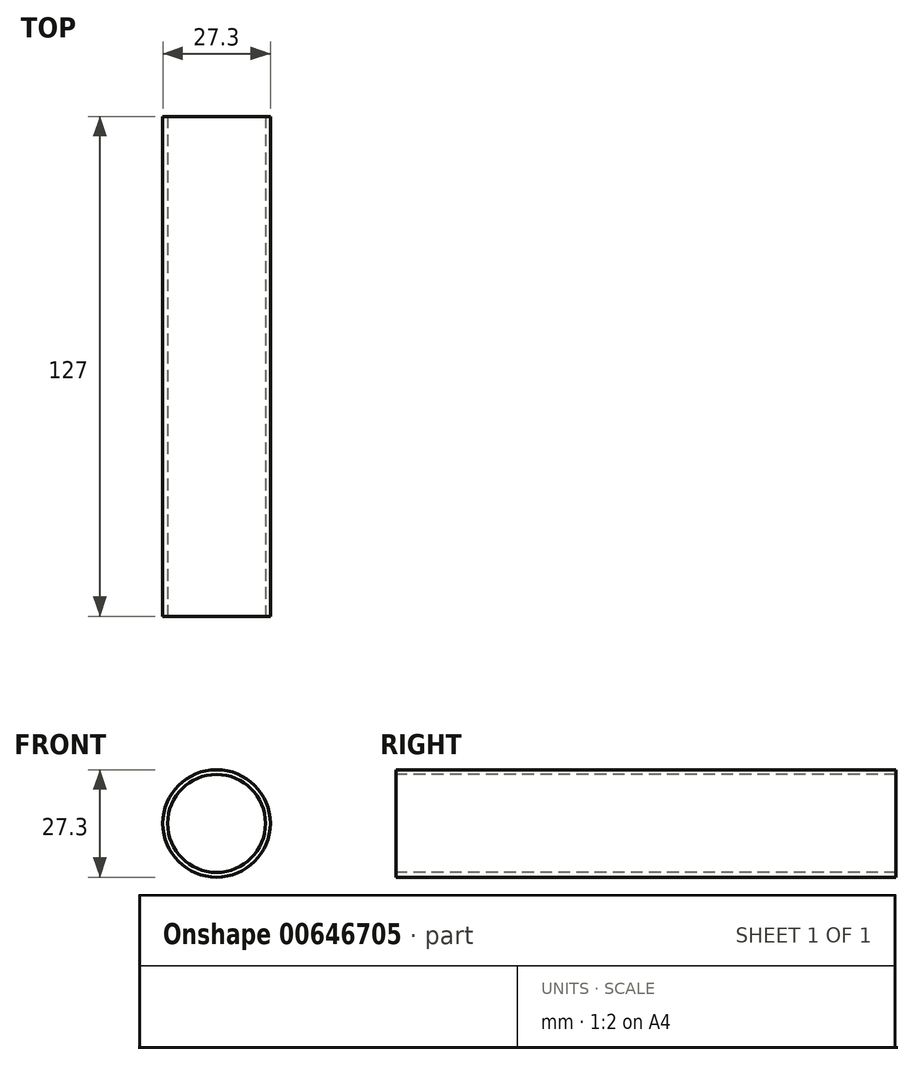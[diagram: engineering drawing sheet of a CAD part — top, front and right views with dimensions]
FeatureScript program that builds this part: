
annotation { "Feature Type Name" : "Feature", "Feature Type Description" : "" }
export const myFeature = defineFeature(function(context is Context, id is Id, definition is map)
    precondition{}
    {
        {
            var Q0;
            Q0=qCreatedBy(makeId("Front.planeOp"),FACE);
            var sketch = newSketch(context, id + "F0", { "sketchPlane" : qUnion([Q0])});
            skCircle(sketch, "E0", {"center": v(0, 0) * mm, "radius": 13.65 * mm});
            skCircle(sketch, "E1", {"center": v(0, 0) * mm, "radius": 12.45 * mm});
            skSolve(sketch);
        }
        {
            var Q0;
            Q0=sQuery(id+"F0.wireOp",EDGE,"E1");
            var Q1;
            Q1=sQuery(id+"F0.wireOp",EDGE,"E0");
            extrude(context, id + "F1", {"bodyType" : ToolBodyType.SURFACE, "surfaceEntities" : qUnion([Q0, Q1]), "depth" : 127 * mm, "offsetDistance" : 25.4 * mm});
        }
    });
